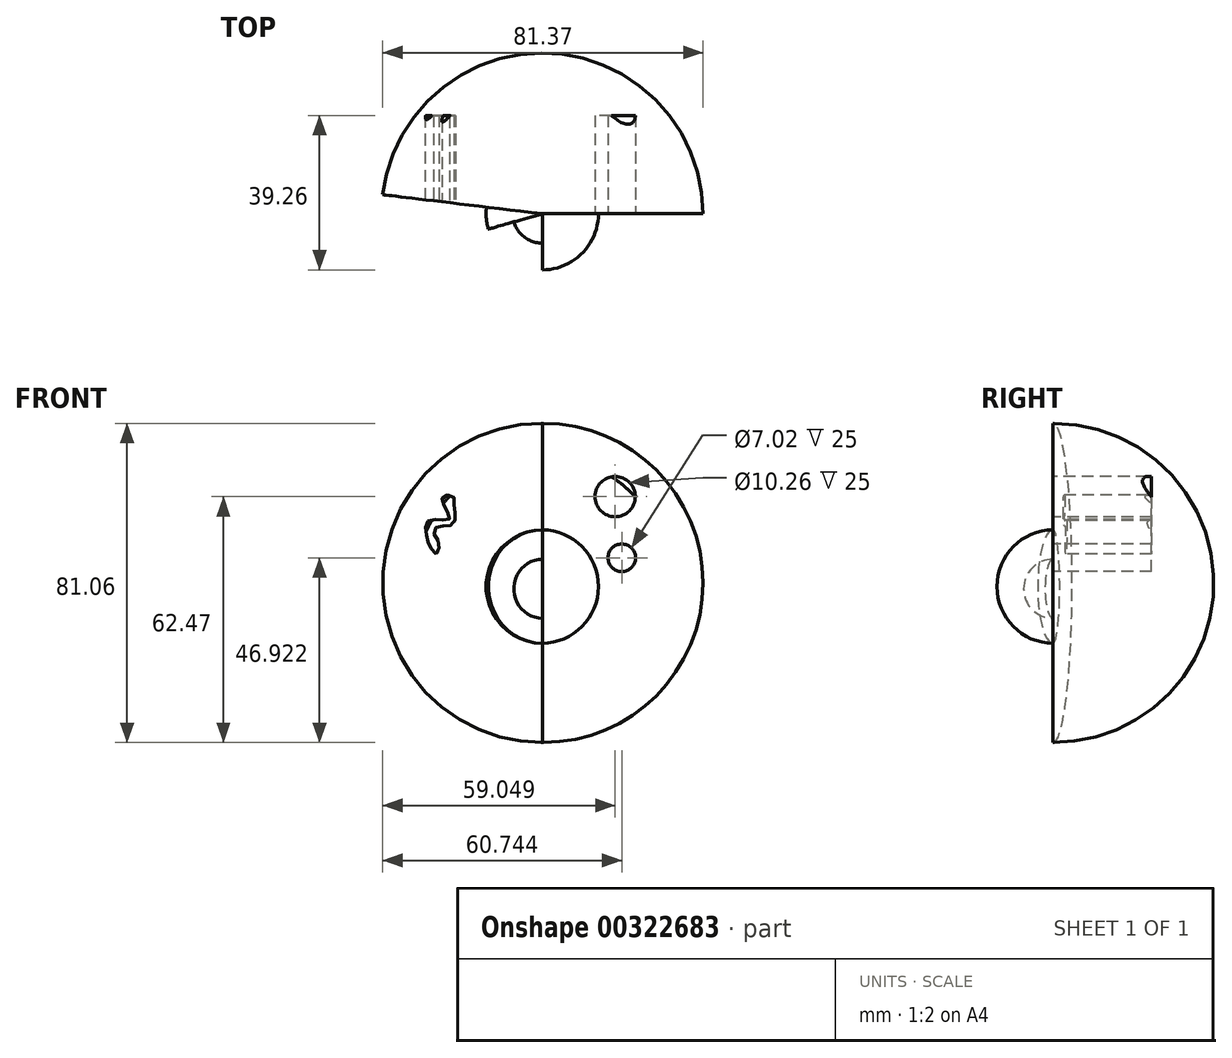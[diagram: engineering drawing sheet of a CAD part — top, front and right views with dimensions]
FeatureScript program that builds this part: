
annotation { "Feature Type Name" : "Feature", "Feature Type Description" : "" }
export const myFeature = defineFeature(function(context is Context, id is Id, definition is map)
    precondition{}
    {
        {
            var Q0;
            Q0=qCreatedBy(makeId("Right.planeOp"),FACE);
            var sketch = newSketch(context, id + "F0", { "sketchPlane" : qUnion([Q0])});
            skLineSegment(sketch, "E0", {"start": v(0, 0) * mm, "end": v(0, 15) * mm});
            skArc(sketch, "E1", {"start": v(0, 15) * mm, "mid": v(-7.48, 7.5) * mm, "end": v(0, 0) * mm});
            skSolve(sketch);
        }
        {
            var Q0;
            Q0 = qSketchRegion(id + "F0", true);
            var Q1;
            Q1=sQuery(id+"F0.wireOp",EDGE,"E0");
            revolve(context, id + "F1", {"entities" : qUnion([Q0]), "axis" : qUnion([Q1]), "revolveType" : RevolveType.FULL});
        }
        {
            var Q0;
            Q0=qCreatedBy(makeId("Right.planeOp"),FACE);
            var sketch = newSketch(context, id + "F2", { "sketchPlane" : qUnion([Q0])});
            skLineSegment(sketch, "E2", {"start": v(0, -6.38) * mm, "end": v(0, 22.48) * mm});
            skArc(sketch, "E3", {"start": v(0, 22.48) * mm, "mid": v(-14.26, 8.05) * mm, "end": v(0, -6.38) * mm});
            skSolve(sketch);
        }
        {
            var Q0;
            Q0 = qSketchRegion(id + "F2", true);
            var Q1;
            Q1=sQuery(id+"F2.wireOp",EDGE,"E2");
            revolve(context, id + "F3", {"operationType" : NewBodyOperationType.ADD, "entities" : qUnion([Q0]), "axis" : qUnion([Q1]), "revolveType" : RevolveType.ONE_DIRECTION, "angle" : 285.85 * degree});
        }
        {
            var Q0;
            Q0=qCreatedBy(makeId("Front.planeOp"),FACE);
            var sketch = newSketch(context, id + "F4", { "sketchPlane" : qUnion([Q0])});
            skLineSegment(sketch, "E4", {"start": v(0, 49.51) * mm, "end": v(0, -31.55) * mm});
            skArc(sketch, "E5", {"start": v(0, -31.55) * mm, "mid": v(40.83, 8.98) * mm, "end": v(0, 49.51) * mm});
            skSolve(sketch);
        }
        {
            var Q0;
            Q0 = qSketchRegion(id + "F4", true);
            var Q1;
            Q1=sQuery(id+"F4.wireOp",EDGE,"E4");
            revolve(context, id + "F5", {"operationType" : NewBodyOperationType.ADD, "entities" : qUnion([Q0]), "axis" : qUnion([Q1]), "revolveType" : RevolveType.ONE_DIRECTION, "oppositeDirection" : true, "angle" : 173.18 * degree});
        }
        {
            var Q0;
            Q0=qCreatedBy(makeId("Front.planeOp"),FACE);
            var sketch = newSketch(context, id + "F6", { "sketchPlane" : qUnion([Q0])});
            skFitSpline(sketch, "E6", {"points": [v(-27.04, 16.28) * mm, v(-29.19, 24.49) * mm, v(-23.58, 25.15) * mm, v(-25.46, 30.63) * mm, v(-22.5, 30.8) * mm, v(-22.42, 29.35) * mm, v(-22.32, 27.55) * mm, v(-22.58, 23.93) * mm, v(-26.78, 23.17) * mm, v(-27.64, 21.78) * mm, v(-26.4, 19.4) * mm, v(-27.04, 16.28) * mm]});
            skSolve(sketch);
        }
        {
            var Q0;
            Q0=makeQuery(id+"F5.opRevolve","CAP_FACE",FACE,{"disambiguationData":[OSD([sQuery(id+"F4.wireOp",EDGE,"E4"),sQuery(id+"F4.wireOp",EDGE,"E5")])],"isStart":true});
            var sketch = newSketch(context, id + "F7", { "sketchPlane" : qUnion([Q0])});
            skSolve(sketch);
        }
        {
            var Q0;
            Q0=qCreatedBy(makeId("Front.planeOp"),FACE);
            var sketch = newSketch(context, id + "F8", { "sketchPlane" : qUnion([Q0])});
            skFitSpline(sketch, "E7", {"points": [v(9.93, -10.1) * mm, v(14.7, -3.16) * mm, v(16.76, 0) * mm, v(19.34, 3.93) * mm, v(20.38, 0) * mm, v(18.13, -3.38) * mm, v(16.46, -7.03) * mm, v(14.16, -9.62) * mm], "startDerivative": vector(27.54, 40.74) * mm, "endDerivative": vector(-20.6, -18.65) * mm});
            skFitSpline(sketch, "E8", {"points": [v(20.12, -4.73) * mm, v(14.16, -9.62) * mm, v(14.16, -12.77) * mm], "startDerivative": vector(-12.74, -8) * mm, "endDerivative": vector(1.9, -8.08) * mm});
            skFitSpline(sketch, "E9", {"points": [v(13.92, -11.72) * mm, v(14.7, -3.16) * mm, v(20.38, 0) * mm, v(20.38, -3.16) * mm, v(17.53, -6.36) * mm, v(15.02, -8.85) * mm, v(15.02, -13.52) * mm], "startDerivative": vector(-6.2, 41.83) * mm, "endDerivative": vector(4.82, -32.1) * mm});
            skFitSpline(sketch, "E10", {"points": [v(22.52, -3.56) * mm, v(23.86, 0.38) * mm, v(23.65, 0) * mm, v(21.42, -6.08) * mm], "startDerivative": vector(5.28, 14.8) * mm, "endDerivative": vector(-5.53, -15.7) * mm});
            skFitSpline(sketch, "E11", {"points": [v(18.56, -12.78) * mm, v(20.6, -10.8) * mm, v(18.77, -9.7) * mm, v(18.26, -5.91) * mm, v(23.2, -1.64) * mm, v(22.52, -3.56) * mm], "startDerivative": vector(17.53, 12.38) * mm, "endDerivative": vector(-9.64, -17.3) * mm});
            skCircle(sketch, "E12", {"center": v(15.9, 24.98) * mm, "radius": 1.66 * mm});
            skCircle(sketch, "E13", {"center": v(20.2, 15.37) * mm, "radius": 3.5 * mm});
            skSolve(sketch);
        }
        {
            var Q0;
            Q0=makeQuery(id+"F8.imprint","IMPRINT",FACE,{"disambiguationData":[TD([[makeQuery(id+"F8.imprint","IMPRINT",EDGE,{"derivedFrom":sQuery(id+"F8.wireOp",EDGE,"E13")}),1.0]])]});
            extrude(context, id + "F9", {"entities" : qUnion([Q0]), "operationType" : NewBodyOperationType.REMOVE, "oppositeDirection" : true, "depth" : 25 * mm});
        }
        {
            var Q0;
            Q0 = qSketchRegion(id + "F6", true);
            extrude(context, id + "F10", {"entities" : qUnion([Q0]), "operationType" : NewBodyOperationType.REMOVE, "oppositeDirection" : true, "depth" : 25 * mm});
        }
        {
            var Q0;
            Q0=qCreatedBy(makeId("Front.planeOp"),FACE);
            var sketch = newSketch(context, id + "F11", { "sketchPlane" : qUnion([Q0])});
            skCircle(sketch, "E14", {"center": v(18.5, 30.92) * mm, "radius": 5.13 * mm});
            skSolve(sketch);
        }
        {
            var Q0;
            Q0=makeQuery(id+"F11.imprint","IMPRINT",FACE,{"disambiguationData":[TD([[makeQuery(id+"F11.imprint","IMPRINT",EDGE,{"derivedFrom":sQuery(id+"F11.wireOp",EDGE,"E14")}),1.0]])]});
            extrude(context, id + "F12", {"entities" : qUnion([Q0]), "operationType" : NewBodyOperationType.REMOVE, "oppositeDirection" : true, "depth" : 25 * mm});
        }
    });
